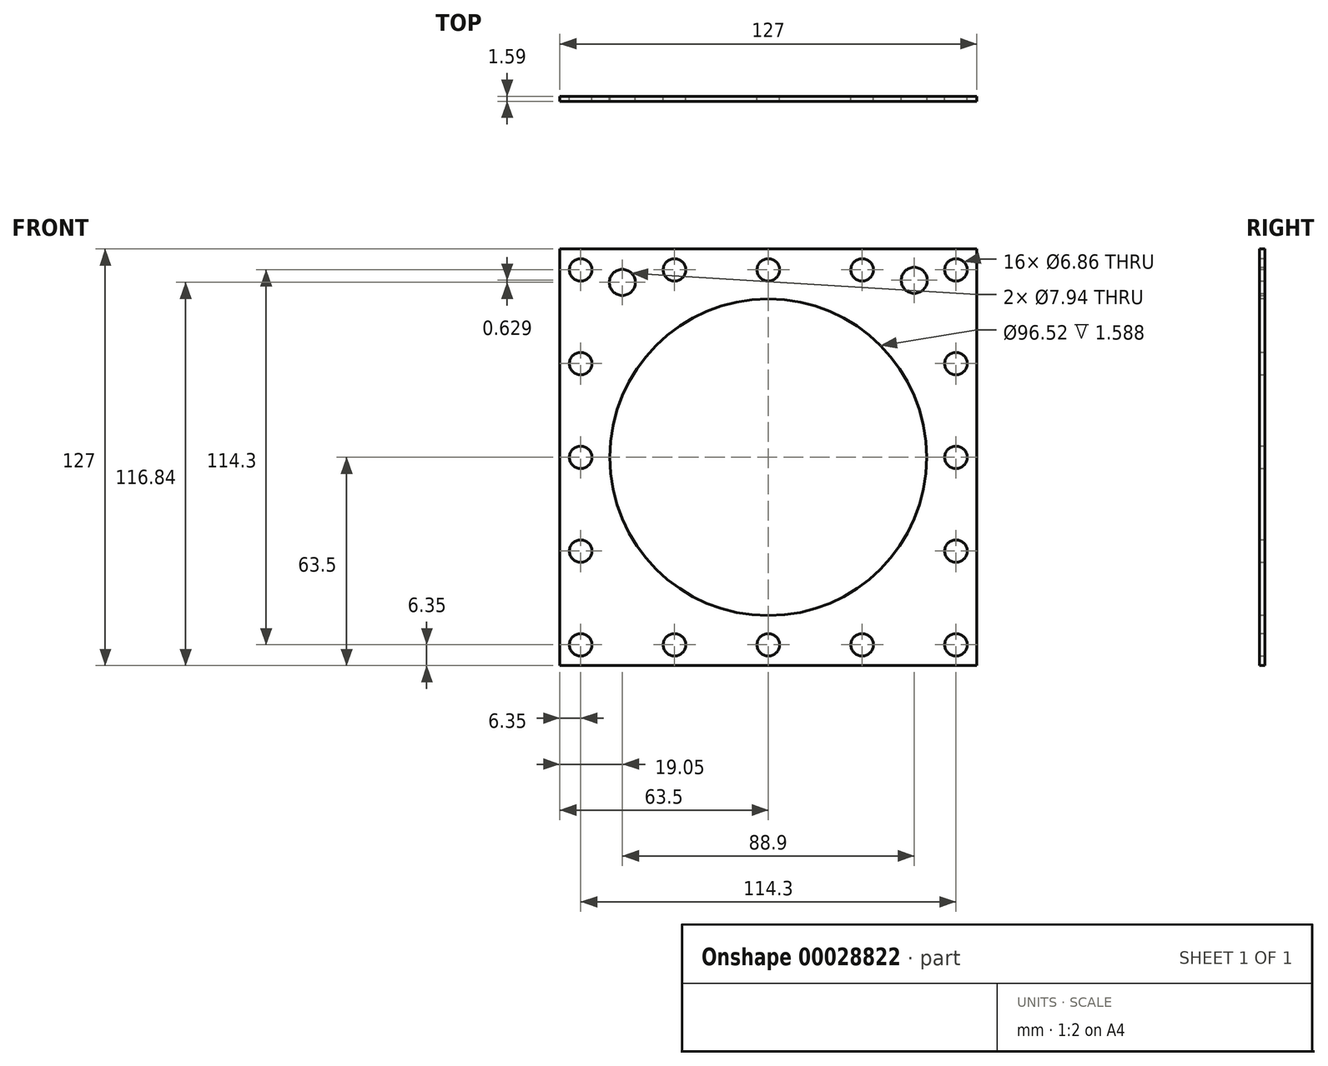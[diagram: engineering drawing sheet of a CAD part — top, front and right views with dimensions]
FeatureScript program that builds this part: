
annotation { "Feature Type Name" : "Feature", "Feature Type Description" : "" }
export const myFeature = defineFeature(function(context is Context, id is Id, definition is map)
    precondition{}
    {
        {
            var Q0;
            Q0=qCreatedBy(makeId("Front.planeOp"),FACE);
            var sketch = newSketch(context, id + "F0", { "sketchPlane" : qUnion([Q0])});
            skLineSegment(sketch, "E0.rect.bottom", {"start": v(63.5, 63.5) * mm, "end": v(-63.5, 63.5) * mm});
            skLineSegment(sketch, "E0.rect.top", {"start": v(63.5, -63.5) * mm, "end": v(-63.5, -63.5) * mm});
            skLineSegment(sketch, "E0.rect.left", {"start": v(63.5, 63.5) * mm, "end": v(63.5, -63.5) * mm});
            skLineSegment(sketch, "E0.rect.right", {"start": v(-63.5, 63.5) * mm, "end": v(-63.5, -63.5) * mm});
            skPoint(sketch, "E0.rect.middle", {"position": v(0, 0) * mm});
            skCircle(sketch, "E1", {"center": v(-44.45, 53.34) * mm, "radius": 3.97 * mm});
            skCircle(sketch, "E2", {"center": v(0, 0) * mm, "radius": 47.56 * mm, "construction": true});
            skLineSegment(sketch, "E3.rect.bottom", {"start": v(-57.15, 57.15) * mm, "end": v(57.15, 57.15) * mm, "construction": true});
            skLineSegment(sketch, "E3.rect.top", {"start": v(-57.15, -57.15) * mm, "end": v(57.15, -57.15) * mm, "construction": true});
            skLineSegment(sketch, "E3.rect.left", {"start": v(-57.15, 57.15) * mm, "end": v(-57.15, -57.15) * mm, "construction": true});
            skLineSegment(sketch, "E3.rect.right", {"start": v(57.15, 57.15) * mm, "end": v(57.15, -57.15) * mm, "construction": true});
            skPoint(sketch, "E4", {"position": v(0, 57.15) * mm});
            skPoint(sketch, "E5", {"position": v(57.15, 0) * mm});
            skPoint(sketch, "E6", {"position": v(0, -57.15) * mm});
            skPoint(sketch, "E7", {"position": v(-57.15, 0) * mm});
            skCircle(sketch, "E8", {"center": v(-57.15, 57.15) * mm, "radius": 3.43 * mm});
            skCircle(sketch, "E9", {"center": v(0, 57.15) * mm, "radius": 3.43 * mm});
            skCircle(sketch, "E10", {"center": v(57.15, 57.15) * mm, "radius": 3.43 * mm});
            skCircle(sketch, "E11", {"center": v(57.15, 0) * mm, "radius": 3.43 * mm});
            skCircle(sketch, "E12", {"center": v(57.15, -57.15) * mm, "radius": 3.43 * mm});
            skCircle(sketch, "E13", {"center": v(0, -57.15) * mm, "radius": 3.43 * mm});
            skCircle(sketch, "E14", {"center": v(-57.15, -57.15) * mm, "radius": 3.43 * mm});
            skCircle(sketch, "E15", {"center": v(-57.15, 0) * mm, "radius": 3.43 * mm});
            skLineSegment(sketch, "E16.rect.bottom", {"start": v(-50, 50) * mm, "end": v(50, 50) * mm, "construction": true});
            skLineSegment(sketch, "E16.rect.top", {"start": v(-50, -50) * mm, "end": v(50, -50) * mm, "construction": true});
            skLineSegment(sketch, "E16.rect.left", {"start": v(-50, 50) * mm, "end": v(-50, -50) * mm, "construction": true});
            skLineSegment(sketch, "E16.rect.right", {"start": v(50, 50) * mm, "end": v(50, -50) * mm, "construction": true});
            skCircle(sketch, "E17", {"center": v(28.57, 57.15) * mm, "radius": 3.43 * mm});
            skCircle(sketch, "E18", {"center": v(57.15, 28.58) * mm, "radius": 3.43 * mm});
            skCircle(sketch, "E19", {"center": v(57.15, -28.58) * mm, "radius": 3.43 * mm});
            skCircle(sketch, "E20", {"center": v(28.58, -57.15) * mm, "radius": 3.43 * mm});
            skCircle(sketch, "E21", {"center": v(-28.58, -57.15) * mm, "radius": 3.43 * mm});
            skCircle(sketch, "E22", {"center": v(-57.15, -28.58) * mm, "radius": 3.43 * mm});
            skCircle(sketch, "E23", {"center": v(-57.15, 28.58) * mm, "radius": 3.43 * mm});
            skCircle(sketch, "E24", {"center": v(-28.58, 57.15) * mm, "radius": 3.43 * mm});
            skCircle(sketch, "E25", {"center": v(44.45, 53.97) * mm, "radius": 3.97 * mm});
            skSolve(sketch);
        }
        {
            var Q0;
            Q0=qSketchRegion(id+"F0",true);
            var Q1;
            {var subQ21=sQuery(id+"F0.wireOp",EDGE,"f6949425-b88c-4a0e-8302-07c829dae053.0");var subQ27=sQuery(id+"F0.wireOp",EDGE,"5bd9be1d-ee3e-4944-9718-c5885c81100e");var subQ29=makeQuery(id+"F0.imprint","INTERSECT",VERTEX,{"derivedFrom":[subQ21,subQ27]});Q1=makeQuery(id+"F0.imprint","IMPRINT",FACE,{"disambiguationData":[TD([[makeQuery(id+"F0.imprint","IMPRINT",EDGE,{"disambiguationData":[TD([[subQ29,-1.0]])],"derivedFrom":subQ21}),-1.0]])]});}
            extrude(context, id + "F1", {"entities" : qUnion([Q0, Q1]), "depth" : 1.59 * mm});
        }
        {
            var Q0;
            Q0=makeQuery(id+"F1.opExtrude","CAP_FACE",FACE,{"disambiguationData":[OSD([sQuery(id+"F0.wireOp",EDGE,"E0.rect.bottom"),sQuery(id+"F0.wireOp",EDGE,"E0.rect.top"),sQuery(id+"F0.wireOp",EDGE,"E0.rect.left"),sQuery(id+"F0.wireOp",EDGE,"E0.rect.right"),sQuery(id+"F0.wireOp",EDGE,"1b772a9f-1761-4584-9b2b-9508be88e127"),sQuery(id+"F0.wireOp",EDGE,"5bd9be1d-ee3e-4944-9718-c5885c81100e"),sQuery(id+"F0.wireOp",EDGE,"a4b3396b-acb1-4126-9ecc-f22d3d9e1673"),sQuery(id+"F0.wireOp",EDGE,"6f9071d3-dfce-459a-96f3-6cfad81b1998"),sQuery(id+"F0.wireOp",EDGE,"8e253895-448c-4740-8d73-7ad6095a0958"),sQuery(id+"F0.wireOp",EDGE,"49ddc21f-956a-45ed-accb-e36c5fb570fd"),sQuery(id+"F0.wireOp",EDGE,"4c855955-bd80-4a33-8133-648448e085db"),sQuery(id+"F0.wireOp",EDGE,"5388e59b-5754-40e4-abb9-c8fe2573278b"),sQuery(id+"F0.wireOp",EDGE,"cb97a597-6742-4d9a-a243-e93a22987a54"),sQuery(id+"F0.wireOp",EDGE,"2f3ac294-263d-4671-b671-df59b6b99c8d")])],"isStart":false});
            var sketch = newSketch(context, id + "F2", { "sketchPlane" : qUnion([Q0])});
            skCircle(sketch, "E26", {"center": v(0, 0) * mm, "radius": 48.26 * mm});
            skSolve(sketch);
        }
        {
            var Q0;
            Q0=qSketchRegion(id+"F2",true);
            extrude(context, id + "F3", {"entities" : qUnion([Q0]), "operationType" : NewBodyOperationType.REMOVE, "endBound" : BoundingType.THROUGH_ALL, "oppositeDirection" : true, "depth" : 3.17 * mm});
        }
    });
